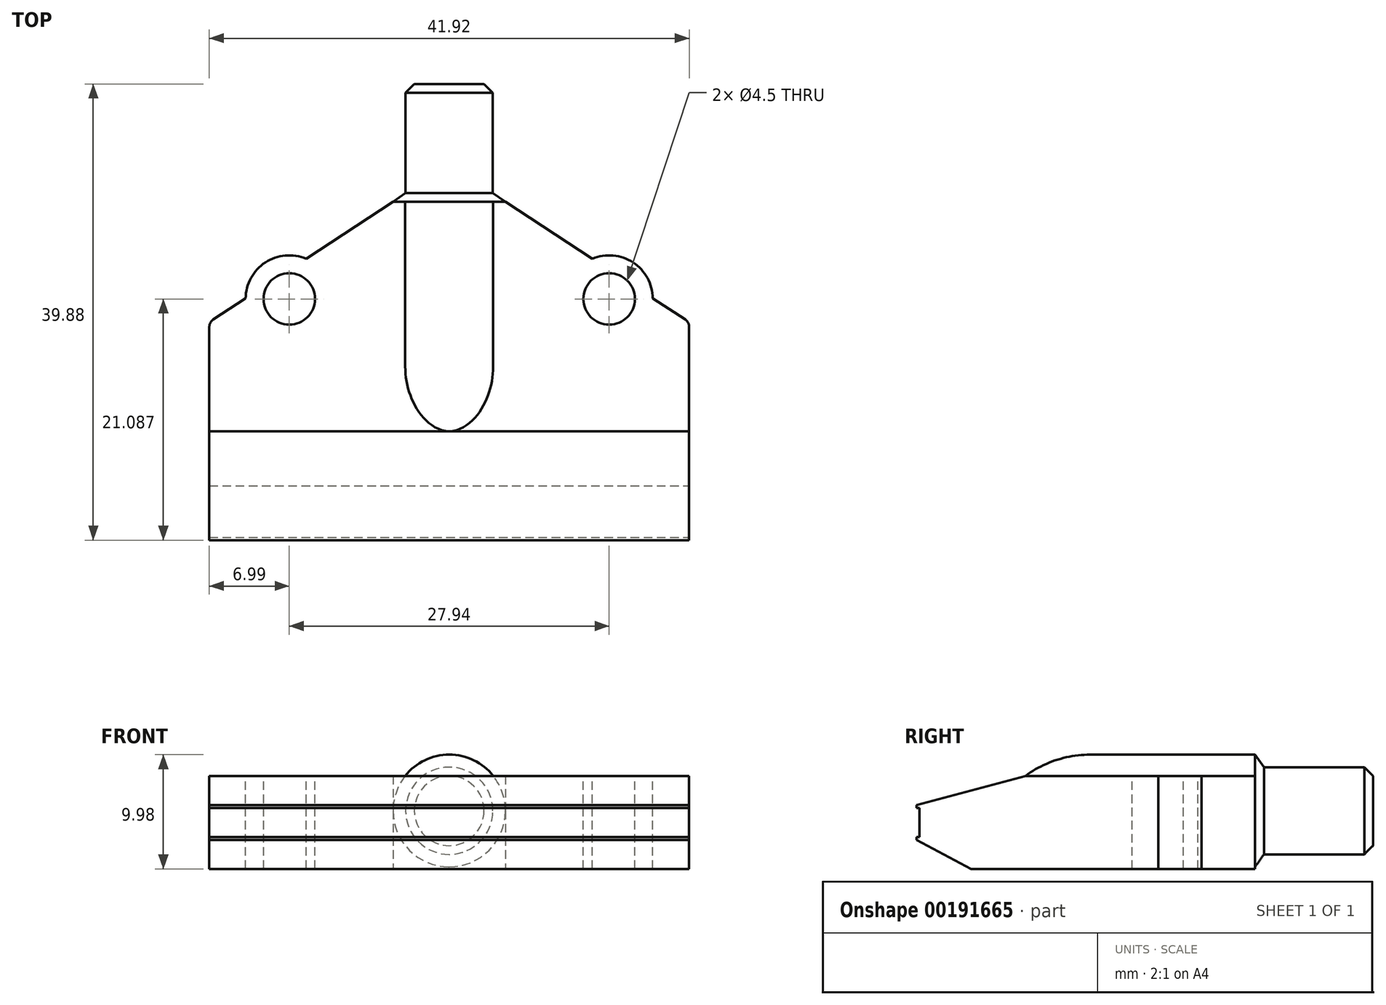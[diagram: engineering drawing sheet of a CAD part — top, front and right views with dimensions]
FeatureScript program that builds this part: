
annotation { "Feature Type Name" : "Feature", "Feature Type Description" : "" }
export const myFeature = defineFeature(function(context is Context, id is Id, definition is map)
    precondition{}
    {
        {
            var Q0;
            Q0=qCreatedBy(makeId("Top.planeOp"),FACE);
            var sketch = newSketch(context, id + "F0", { "sketchPlane" : qUnion([Q0])});
            skLineSegment(sketch, "E0.bottom", {"start": v(-20.95, 9.53) * mm, "end": v(20.96, 9.53) * mm});
            skLineSegment(sketch, "E0.top", {"start": v(-20.96, -9.52) * mm, "end": v(20.95, -9.52) * mm});
            skLineSegment(sketch, "E0.left", {"start": v(-20.96, 9.53) * mm, "end": v(-20.96, -9.52) * mm});
            skLineSegment(sketch, "E0.right", {"start": v(20.96, 9.53) * mm, "end": v(20.95, -9.52) * mm});
            skPoint(sketch, "E0.middle", {"position": v(0, 0) * mm});
            skSolve(sketch);
        }
        {
            var Q0;
            Q0 = qSketchRegion(id + "F0", true);
            extrude(context, id + "F1", {"entities" : qUnion([Q0]), "depth" : 8.13 * mm});
        }
        {
            var Q0;
            Q0=makeQuery(id+"F1.opExtrude","SWEPT_FACE",FACE,{"disambiguationData":[OSD([sQuery(id+"F0.wireOp",EDGE,"E0.right")])]});
            var sketch = newSketch(context, id + "F2", { "sketchPlane" : qUnion([Q0])});
            skLineSegment(sketch, "E1", {"start": v(0, 8.13) * mm, "end": v(-9.53, 5.59) * mm});
            skLineSegment(sketch, "E2", {"start": v(-9.52, 5.59) * mm, "end": v(-9.52, 8.13) * mm});
            skLineSegment(sketch, "E3", {"start": v(-9.52, 8.13) * mm, "end": v(0, 8.13) * mm});
            skLineSegment(sketch, "E4", {"start": v(-9.52, 2.54) * mm, "end": v(-4.76, 0) * mm});
            skLineSegment(sketch, "E5", {"start": v(-4.76, 0) * mm, "end": v(-9.52, 0) * mm});
            skLineSegment(sketch, "E6", {"start": v(-9.52, 0) * mm, "end": v(-9.52, 2.54) * mm});
            skSolve(sketch);
        }
        {
            var Q0;
            Q0 = qSketchRegion(id + "F2", true);
            extrude(context, id + "F3", {"entities" : qUnion([Q0]), "operationType" : NewBodyOperationType.REMOVE, "endBound" : BoundingType.THROUGH_ALL, "oppositeDirection" : true, "depth" : 25.4 * mm});
        }
        {
            var Q0;
            Q0=makeQuery(id+"F1.opExtrude","SWEPT_FACE",FACE,{"disambiguationData":[OSD([sQuery(id+"F0.wireOp",EDGE,"E0.right")])]});
            var sketch = newSketch(context, id + "F4", { "sketchPlane" : qUnion([Q0])});
            skLineSegment(sketch, "E7.bottom", {"start": v(-9.27, 5.33) * mm, "end": v(-9.78, 5.33) * mm});
            skLineSegment(sketch, "E7.top", {"start": v(-9.27, 2.8) * mm, "end": v(-9.78, 2.8) * mm});
            skLineSegment(sketch, "E7.left", {"start": v(-9.27, 5.33) * mm, "end": v(-9.27, 2.8) * mm});
            skLineSegment(sketch, "E7.right", {"start": v(-9.78, 5.33) * mm, "end": v(-9.78, 2.8) * mm});
            skPoint(sketch, "E7.middle", {"position": v(-9.52, 4.06) * mm});
            skSolve(sketch);
        }
        {
            var Q0;
            Q0 = qSketchRegion(id + "F4", true);
            extrude(context, id + "F5", {"entities" : qUnion([Q0]), "operationType" : NewBodyOperationType.REMOVE, "endBound" : BoundingType.THROUGH_ALL, "oppositeDirection" : true, "depth" : 25.4 * mm});
        }
        {
            var Q0;
            Q0=qCreatedBy(makeId("Right.planeOp"),FACE);
            var sketch = newSketch(context, id + "F6", { "sketchPlane" : qUnion([Q0])});
            skLineSegment(sketch, "E8.0", {"start": v(-9.52, 5.59) * mm, "end": v(-9.52, 5.33) * mm, "construction": true});
            skPoint(sketch, "E9.0", {"position": v(-9.52, 2.67) * mm});
            skLineSegment(sketch, "E10.0", {"start": v(-9.52, 2.8) * mm, "end": v(-9.52, 2.54) * mm, "construction": true});
            skLineSegment(sketch, "E11", {"start": v(-9.52, 5.59) * mm, "end": v(-9.52, 2.54) * mm, "construction": true});
            skLineSegment(sketch, "E12", {"start": v(-9.52, 5.08) * mm, "end": v(30.35, 5.08) * mm, "construction": true});
            skPoint(sketch, "E12.endSnap0", {"position": v(-9.52, 5.08) * mm});
            skLineSegment(sketch, "E13", {"start": v(30.35, 5.08) * mm, "end": v(30.35, 8.9) * mm});
            skLineSegment(sketch, "E14", {"start": v(30.35, 8.9) * mm, "end": v(20.83, 8.9) * mm});
            skLineSegment(sketch, "E15", {"start": v(20.83, 8.9) * mm, "end": v(20.05, 9.98) * mm});
            skLineSegment(sketch, "E16", {"start": v(20.05, 9.98) * mm, "end": v(5.65, 9.98) * mm});
            skPoint(sketch, "E17.0", {"position": v(0, 8.13) * mm});
            skArc(sketch, "E18", {"start": v(5.65, 9.98) * mm, "mid": v(2.68, 9.5) * mm, "end": v(0, 8.13) * mm});
            skLineSegment(sketch, "E19", {"start": v(0, 8.13) * mm, "end": v(0, 5.08) * mm});
            skLineSegment(sketch, "E20", {"start": v(0, 5.08) * mm, "end": v(30.35, 5.08) * mm});
            skSolve(sketch);
        }
        {
            var Q0;
            Q0=makeQuery(id+"F6.imprint","IMPRINT",FACE,{"disambiguationData":[TD([[makeQuery(id+"F6.imprint","IMPRINT",EDGE,{"derivedFrom":sQuery(id+"F6.wireOp",EDGE,"E13")}),1.0]])]});
            var Q1;
            Q1=sQuery(id+"F6.wireOp",EDGE,"E20");
            revolve(context, id + "F7", {"operationType" : NewBodyOperationType.ADD, "entities" : qUnion([Q0]), "axis" : qUnion([Q1]), "revolveType" : RevolveType.FULL});
        }
        {
            var Q0;
            Q0=makeQuery(id+"F7.opRevolve","SWEPT_FACE",FACE,{"disambiguationData":[OSD([sQuery(id+"F6.wireOp",EDGE,"E13")])]});
            chamfer(context, id + "F8", {"entities" : qUnion([Q0]), "width" : 0.76 * mm, "tangentPropagation" : true});
        }
        {
            var Q0;
            Q0=qCreatedBy(makeId("Top.planeOp"),FACE);
            var sketch = newSketch(context, id + "F9", { "sketchPlane" : qUnion([Q0])});
            skLineSegment(sketch, "E21.0", {"start": v(3.84, 9.53) * mm, "end": v(20.96, 9.53) * mm});
            skPoint(sketch, "E22.0", {"position": v(-12.4, 9.53) * mm});
            skLineSegment(sketch, "E23.0", {"start": v(-20.95, 9.53) * mm, "end": v(-3.84, 9.53) * mm});
            skLineSegment(sketch, "E24", {"start": v(-4.9, 9.53) * mm, "end": v(-4.9, 20.05) * mm});
            skLineSegment(sketch, "E25", {"start": v(4.9, 20.05) * mm, "end": v(4.9, 9.53) * mm});
            skLineSegment(sketch, "E26", {"start": v(-20.96, 9.53) * mm, "end": v(20.96, 9.53) * mm});
            skLineSegment(sketch, "E27", {"start": v(20.96, 9.53) * mm, "end": v(4.9, 20.05) * mm});
            skLineSegment(sketch, "E28", {"start": v(-4.9, 20.05) * mm, "end": v(-20.96, 9.53) * mm});
            skLineSegment(sketch, "E29", {"start": v(4.9, 20.05) * mm, "end": v(-4.9, 20.05) * mm});
            skSolve(sketch);
        }
        {
            var Q0;
            Q0 = qSketchRegion(id + "F9", true);
            var Q1;
            {var subQ0=sQuery(id+"F0.wireOp",EDGE,"E0.right");var subQ1=sQuery(id+"F0.wireOp",EDGE,"E0.bottom");var subQ2=makeQuery(id+"F1.opExtrude","CAP_FACE",FACE,{"disambiguationData":[OSD([subQ1,sQuery(id+"F0.wireOp",EDGE,"E0.top"),sQuery(id+"F0.wireOp",EDGE,"E0.left"),subQ0])],"isStart":false});Q1=makeQuery(id+"F7.boolean.opBoolean","SPLIT",FACE,{"disambiguationData":[TD([makeQuery(id+"F1.opExtrude","SWEPT_FACE",FACE,{"disambiguationData":[OSD([subQ0])]})])],"derivedFrom":subQ2});}
            extrude(context, id + "F10", {"entities" : qUnion([Q0]), "operationType" : NewBodyOperationType.ADD, "endBound" : BoundingType.UP_TO_SURFACE, "endBoundEntityFace" : qUnion([Q1]), "depth" : 25.4 * mm});
        }
        {
            var Q0;
            {var subQ0=sQuery(id+"F0.wireOp",EDGE,"E0.right");var subQ1=sQuery(id+"F0.wireOp",EDGE,"E0.bottom");var subQ2=makeQuery(id+"F1.opExtrude","CAP_FACE",FACE,{"disambiguationData":[OSD([subQ1,sQuery(id+"F0.wireOp",EDGE,"E0.top"),sQuery(id+"F0.wireOp",EDGE,"E0.left"),subQ0])],"isStart":false});Q0=makeQuery(id+"F10.boolean.opBoolean","MERGE",FACE,{"derivedFrom":[makeQuery(id+"F7.boolean.opBoolean","SPLIT",FACE,{"disambiguationData":[TD([makeQuery(id+"F1.opExtrude","SWEPT_FACE",FACE,{"disambiguationData":[OSD([subQ0])]})])],"derivedFrom":subQ2}),makeQuery(id+"F10.opExtrude","CAP_FACE",FACE,{"disambiguationData":[OSD([sQuery(id+"F9.wireOp",EDGE,"E26"),sQuery(id+"F9.wireOp",EDGE,"E27"),sQuery(id+"F9.wireOp",EDGE,"E28"),sQuery(id+"F9.wireOp",EDGE,"E29")])],"isStart":false})]});}
            var sketch = newSketch(context, id + "F11", { "sketchPlane" : qUnion([Q0])});
            skLineSegment(sketch, "E30.0", {"start": v(-20.96, -9.52) * mm, "end": v(20.96, -9.52) * mm, "construction": true});
            skLineSegment(sketch, "E31.0", {"start": v(-20.95, 11.56) * mm, "end": v(20.96, 11.56) * mm, "construction": true});
            skLineSegment(sketch, "E32", {"start": v(0, -14.08) * mm, "end": v(0, 15.97) * mm, "construction": true});
            skLineSegment(sketch, "E33.0", {"start": v(13.97, -14.08) * mm, "end": v(13.97, 15.97) * mm, "construction": true});
            skCircle(sketch, "E34", {"center": v(13.97, 11.56) * mm, "radius": 3.81 * mm});
            skCircle(sketch, "E35.MirrorC", {"center": v(-13.97, 11.56) * mm, "radius": 3.81 * mm});
            skSolve(sketch);
        }
        {
            var Q0;
            Q0 = qSketchRegion(id + "F11", true);
            var Q1;
            Q1=makeQuery(id+"F10.boolean.opBoolean","MERGE",FACE,{"derivedFrom":[makeQuery(id+"F1.opExtrude","CAP_FACE",FACE,{"disambiguationData":[OSD([sQuery(id+"F0.wireOp",EDGE,"E0.bottom"),sQuery(id+"F0.wireOp",EDGE,"E0.top"),sQuery(id+"F0.wireOp",EDGE,"E0.left"),sQuery(id+"F0.wireOp",EDGE,"E0.right")])],"isStart":true}),makeQuery(id+"F10.opExtrude","CAP_FACE",FACE,{"disambiguationData":[OSD([sQuery(id+"F9.wireOp",EDGE,"E26"),sQuery(id+"F9.wireOp",EDGE,"E27"),sQuery(id+"F9.wireOp",EDGE,"E28"),sQuery(id+"F9.wireOp",EDGE,"E29")])],"isStart":true})]});
            extrude(context, id + "F12", {"entities" : qUnion([Q0]), "operationType" : NewBodyOperationType.ADD, "endBound" : BoundingType.UP_TO_SURFACE, "oppositeDirection" : true, "endBoundEntityFace" : qUnion([Q1]), "depth" : 25.4 * mm});
        }
        {
            var Q0;
            {var subQ0=sQuery(id+"F0.wireOp",EDGE,"E0.right");var subQ1=sQuery(id+"F0.wireOp",EDGE,"E0.bottom");var subQ2=makeQuery(id+"F1.opExtrude","CAP_FACE",FACE,{"disambiguationData":[OSD([subQ1,sQuery(id+"F0.wireOp",EDGE,"E0.top"),sQuery(id+"F0.wireOp",EDGE,"E0.left"),subQ0])],"isStart":false});Q0=makeQuery(id+"F12.boolean.opBoolean","MERGE",FACE,{"derivedFrom":[makeQuery(id+"F10.boolean.opBoolean","MERGE",FACE,{"derivedFrom":[makeQuery(id+"F7.boolean.opBoolean","SPLIT",FACE,{"disambiguationData":[TD([makeQuery(id+"F1.opExtrude","SWEPT_FACE",FACE,{"disambiguationData":[OSD([subQ0])]})])],"derivedFrom":subQ2}),makeQuery(id+"F10.opExtrude","CAP_FACE",FACE,{"disambiguationData":[OSD([sQuery(id+"F9.wireOp",EDGE,"E26"),sQuery(id+"F9.wireOp",EDGE,"E27"),sQuery(id+"F9.wireOp",EDGE,"E28"),sQuery(id+"F9.wireOp",EDGE,"E29")])],"isStart":false})]}),makeQuery(id+"F12.opExtrude","CAP_FACE",FACE,{"disambiguationData":[OSD([sQuery(id+"F11.wireOp",EDGE,"E34")])],"isStart":true})]});}
            var sketch = newSketch(context, id + "F13", { "sketchPlane" : qUnion([Q0])});
            skPoint(sketch, "E36.0", {"position": v(-13.97, 11.56) * mm});
            skPoint(sketch, "E37.0", {"position": v(13.97, 11.56) * mm});
            skSolve(sketch);
        }
        {
            var Q0;
            Q0=sQuery(id+"F13.wireOp",VERTEX,"E36.0");
            var Q1;
            Q1=sQuery(id+"F13.wireOp",VERTEX,"E37.0");
            var Q2;
            Q2=makeQuery(id+"F1.opExtrude","SWEPT_BODY",BODY,{"disambiguationData":[OSD([sQuery(id+"F0.wireOp",EDGE,"E0.bottom"),sQuery(id+"F0.wireOp",EDGE,"E0.top"),sQuery(id+"F0.wireOp",EDGE,"E0.left"),sQuery(id+"F0.wireOp",EDGE,"E0.right")])]});
            hole(context, id + "F14", {"style" : HoleStyle.SIMPLE, "endStyle" : HoleEndStyle.BLIND, "standardTappedOrClearance" : lookupTablePath({ "standard" : "ISO", "size" : "4.5", "type" : "Drilled" }), "standardBlindInLast" : lookupTablePath({ "standard" : "ISO", "size" : "4.5", "type" : "Drilled" }), "holeDiameter" : 4.5 * mm, "holeDepth" : 38.1 * mm, "locations" : qUnion([Q0, Q1]), "scope" : qUnion([Q2])});
        }
        {
            var Q0;
            Q0=makeQuery(id+"F10.boolean.opBoolean","MERGE",EDGE,{"derivedFrom":[makeQuery(id+"F1.opExtrude","SWEPT_EDGE",EDGE,{"disambiguationData":[OSD([sQuery(id+"F0.wireOp",EDGE,"E0.bottom"),sQuery(id+"F0.wireOp",EDGE,"E0.right")])]}),makeQuery(id+"F10.opExtrude","SWEPT_EDGE",EDGE,{"disambiguationData":[OSD([sQuery(id+"F9.wireOp",EDGE,"E26"),sQuery(id+"F9.wireOp",EDGE,"E27")])]})]});
            var Q1;
            Q1=makeQuery(id+"F10.boolean.opBoolean","MERGE",EDGE,{"derivedFrom":[makeQuery(id+"F1.opExtrude","SWEPT_EDGE",EDGE,{"disambiguationData":[OSD([sQuery(id+"F0.wireOp",EDGE,"E0.bottom"),sQuery(id+"F0.wireOp",EDGE,"E0.left")])]}),makeQuery(id+"F10.opExtrude","SWEPT_EDGE",EDGE,{"disambiguationData":[OSD([sQuery(id+"F9.wireOp",EDGE,"E26"),sQuery(id+"F9.wireOp",EDGE,"E28")])]})]});
            fillet(context, id + "F15", {"entities" : qUnion([Q0, Q1]), "radius" : 0.76 * mm, "tangentPropagation" : true, "allowEdgeOverflow" : false});
        }
    });
